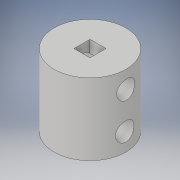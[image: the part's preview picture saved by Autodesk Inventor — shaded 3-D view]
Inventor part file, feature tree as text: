
AUTODESK INVENTOR PART (.ipt)
format: ipt  version: 2018 (Build 220112000, 112)  size: 143,872 bytes
history: native  units: in
note: dims shown in document units (in); Inventor stores cm internally (conversion verified against a paired STEP export)
features: extrude x3, sketch x3
ambient origin geometry x8: Origin, YZ Plane, XZ Plane, XY Plane, X Axis, Y Axis, Z Axis, Center Point
bodies: Solid1 (feature_tree)
feature tree (6):
  extrude  "Extrusion1"  Depth=0.75in
  extrude  "Extrusion2"  Depth=0.375in
  extrude  "Extrusion3"  Depth=0.1925in
  sketch  "Sketch1"  dims[d0=0.1675in d1=0.75in]
  sketch  "Sketch2"  dims[d2=0.375in d3=0.0in d4=0.375in]
  sketch  "Sketch3"  dims[d5=0.375in d6=0.0in d7=0.1925in d8=0.1925in d9=0.75in d10=0.0in]
